# Revit family: Geometric_Sofa_BIM
name_source: partatom
category: Arredi
units: mm (PartAtom-declared; Revit-internal decimal feet)

## family parameters
Attiva taglio nelle viste = No
Basato su piano di lavoro = No
Condiviso = No
Numero OmniClass = 23.40.20.00
Origine composizione di rendering = Geometria famiglia
Punto di calcolo locali = No
Sempre verticale = Sì
Taglio con vuoti quando caricato = No
Titolo OmniClass = General Furniture and Specialties

## types (1)
- CB-458
    AVAILABLE FINISHES = Ebonized black lacquer on Ash (EB) or bleached, white pigment, matte acrylic on Ash (BL). Raw effect lacquer on Oak (RE). Hand rubbed natural oil on Oak or Walnut (NA), or hand rubbed black oil on Walnut (BO). Frame: Satin nickel (SN), satin brass (SB), bronze (BZ) or gunmetal (GM) nanoceramic coated tubular steel.
    BASE MATERIAL = BASSAM_FELLOWS_OAK_O-NA
    BIM BADGE = https://bim.archiproducts.com
    COLLECTION = Geometric
    DEPTH = 720 mm
    Descrizione = Upholstered leather, wood and steel sofa
    FEET MATERIAL = BASSAM_FELLOWS_BRONZE_BZ
    HEIGHT = 705 mm
    MATERIAL DESCRIPTION = Carved solid wood seat, natural Vienna Cane mesh. Tubular stainless steel frame. Upholstery: foam with inverted seam and knife edge with double topstitch.
    Modello = Geometric Sofa
    PRODUCT CODE = CB-458
    PRODUCT SHEET = https://www.archiproducts.com
    Produttore = BassamFellows
    Prospetto di default = 0 mm  [stored 0 ft]
    TECHNICAL SHEET = https://bassamfellows.com
    UPHOLSTERY MATERIAL = BASSAM_FELLOWS_ELEGANT_LEATHER_48027_OLIVE
    URL = https://bassamfellows.com
    WIDTH = 1400 mm  [stored 4.59318 ft]

note: [stored X ft] marks values corroborated as IEEE doubles in the binary element streams (Revit-internal decimal feet)

## geometry (parser evidence)
native form markers: Sweep x2
no freeform markers — native parametric forms only
